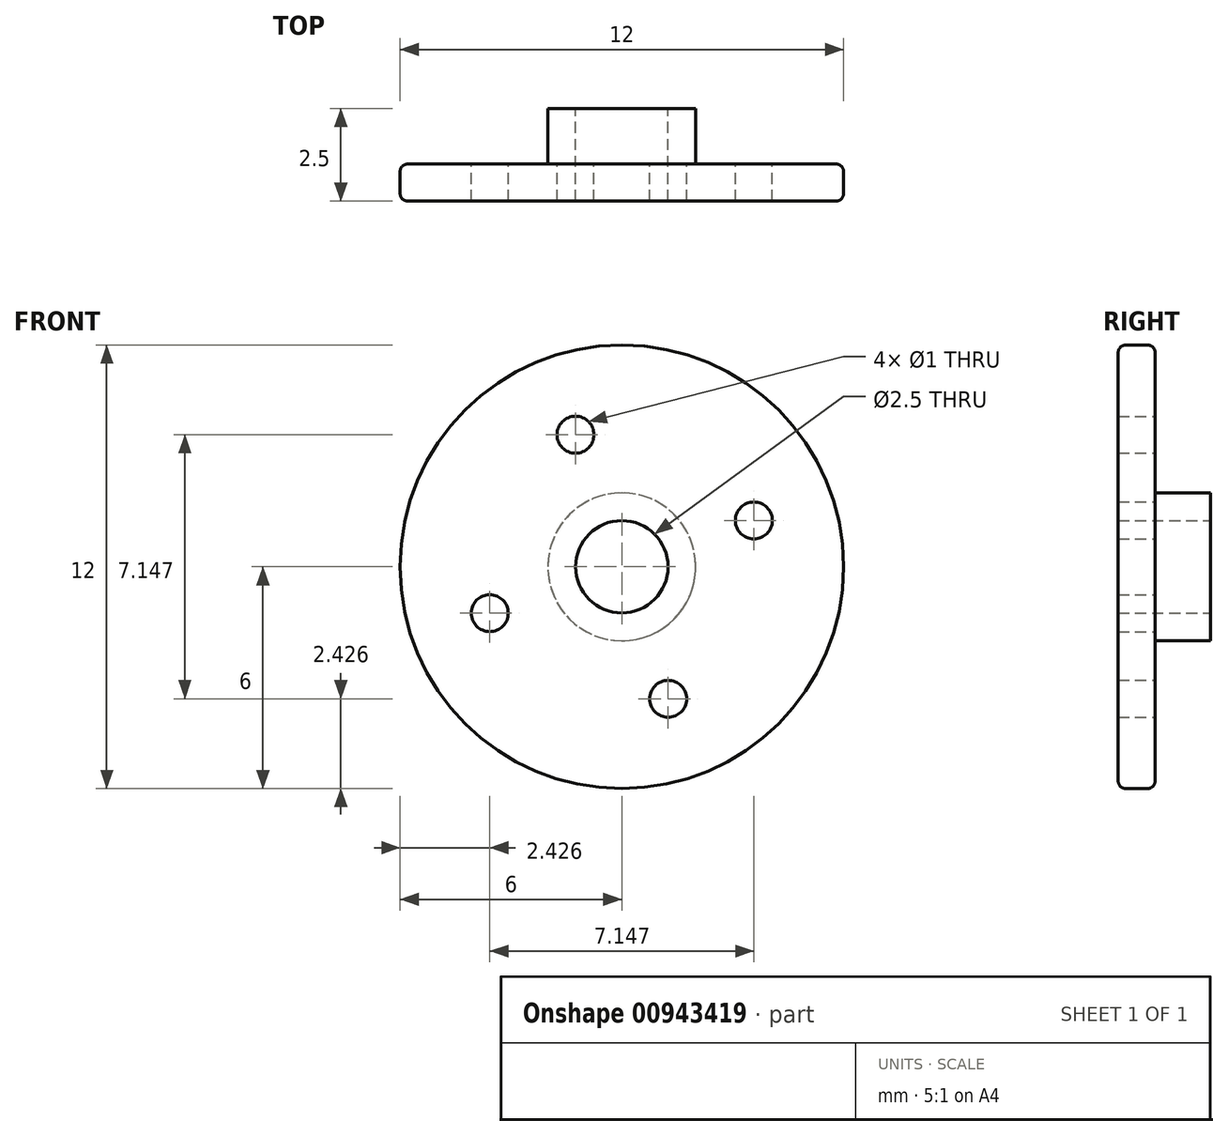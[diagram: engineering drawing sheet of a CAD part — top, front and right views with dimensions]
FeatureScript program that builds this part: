
annotation { "Feature Type Name" : "Feature", "Feature Type Description" : "" }
export const myFeature = defineFeature(function(context is Context, id is Id, definition is map)
    precondition{}
    {
        {
            var Q0;
            Q0=qCreatedBy(makeId("Front.planeOp"),FACE);
            var sketch = newSketch(context, id + "F0", { "sketchPlane" : qUnion([Q0])});
            skCircle(sketch, "E0", {"center": v(0, 0) * mm, "radius": 6 * mm});
            skCircle(sketch, "E1", {"center": v(0, 0) * mm, "radius": 1.25 * mm});
            skCircle(sketch, "E2", {"center": v(-1.25, 3.57) * mm, "radius": 0.5 * mm});
            skCircle(sketch, "E3.1.0", {"center": v(-3.57, -1.25) * mm, "radius": 0.5 * mm});
            skCircle(sketch, "E3.2.0", {"center": v(1.25, -3.57) * mm, "radius": 0.5 * mm});
            skCircle(sketch, "E3.3.0", {"center": v(3.57, 1.25) * mm, "radius": 0.5 * mm});
            skSolve(sketch);
        }
        {
            var Q0;
            Q0 = qSketchRegion(id + "F0", true);
            extrude(context, id + "F1", {"entities" : qUnion([Q0]), "depth" : 1 * mm, "offsetDistance" : 25 * mm});
        }
        {
            var Q0;
            Q0=makeQuery(id+"F1.opExtrude","CAP_EDGE",EDGE,{"disambiguationData":[OSD([sQuery(id+"F0.wireOp",EDGE,"E0")])],"isStart":true});
            var Q1;
            Q1=makeQuery(id+"F1.opExtrude","CAP_EDGE",EDGE,{"disambiguationData":[OSD([sQuery(id+"F0.wireOp",EDGE,"E0")])],"isStart":false});
            fillet(context, id + "F2", {"entities" : qUnion([Q0, Q1]), "radius" : 0.2 * mm, "tangentPropagation" : true, "allowEdgeOverflow" : false});
        }
        {
            var Q0;
            Q0=makeQuery(id+"F1.opExtrude","CAP_FACE",FACE,{"disambiguationData":[OSD([sQuery(id+"F0.wireOp",EDGE,"E0"),sQuery(id+"F0.wireOp",EDGE,"E1"),sQuery(id+"F0.wireOp",EDGE,"rYR10Qx4-efaD-2T1o-SCd4-3g6EwR9dbxhi"),sQuery(id+"F0.wireOp",EDGE,"04d67e72-f369-40b8-96e0-564f40d45e39.1.0"),sQuery(id+"F0.wireOp",EDGE,"04d67e72-f369-40b8-96e0-564f40d45e39.2.0"),sQuery(id+"F0.wireOp",EDGE,"04d67e72-f369-40b8-96e0-564f40d45e39.3.0"),sQuery(id+"F0.wireOp",EDGE,"04d67e72-f369-40b8-96e0-564f40d45e39.4.0"),sQuery(id+"F0.wireOp",EDGE,"04d67e72-f369-40b8-96e0-564f40d45e39.5.0"),sQuery(id+"F0.wireOp",EDGE,"04d67e72-f369-40b8-96e0-564f40d45e39.6.0"),sQuery(id+"F0.wireOp",EDGE,"04d67e72-f369-40b8-96e0-564f40d45e39.7.0")])],"isStart":true});
            var sketch = newSketch(context, id + "F3", { "sketchPlane" : qUnion([Q0])});
            skCircle(sketch, "E4", {"center": v(0, 0) * mm, "radius": 2 * mm});
            skCircle(sketch, "E5", {"center": v(0, 0) * mm, "radius": 1.25 * mm});
            skSolve(sketch);
        }
        {
            var Q0;
            Q0 = qSketchRegion(id + "F3", true);
            extrude(context, id + "F4", {"entities" : qUnion([Q0]), "operationType" : NewBodyOperationType.ADD, "depth" : 1.5 * mm, "offsetDistance" : 25 * mm});
        }
    });
